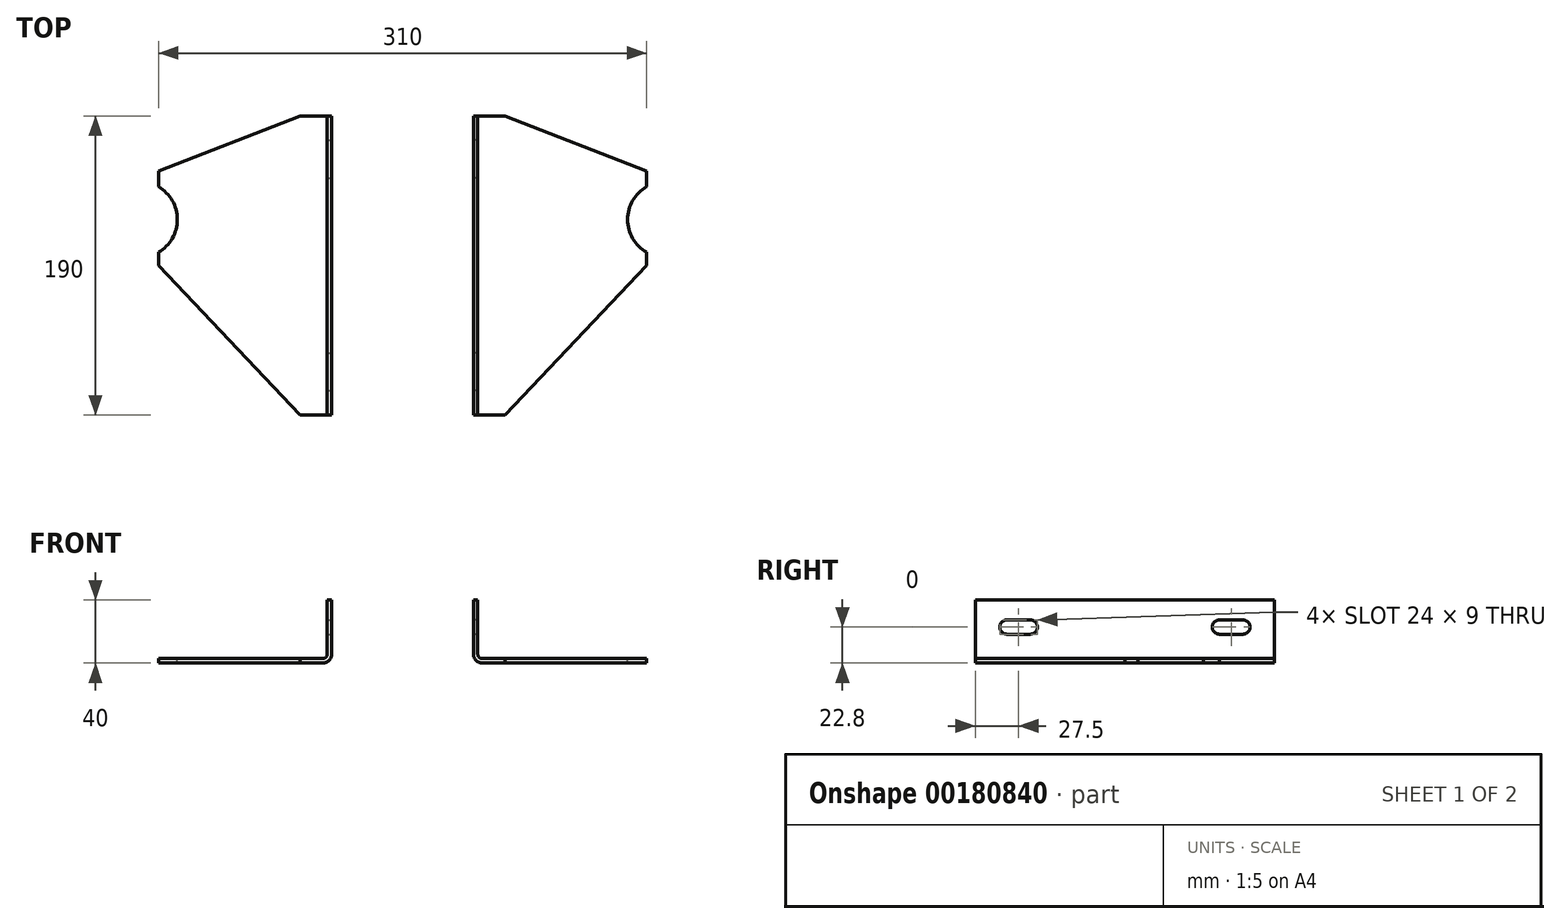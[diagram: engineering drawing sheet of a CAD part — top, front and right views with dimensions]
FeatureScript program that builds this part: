
annotation { "Feature Type Name" : "Feature", "Feature Type Description" : "" }
export const myFeature = defineFeature(function(context is Context, id is Id, definition is map)
    precondition{}
    {
        {
            var Q0;
            Q0=qCreatedBy(makeId("Front.planeOp"),FACE);
            var sketch = newSketch(context, id + "F0", { "sketchPlane" : qUnion([Q0])});
            skLineSegment(sketch, "E0", {"start": v(0, 0) * mm, "end": v(-55, 0) * mm});
            skLineSegment(sketch, "E1", {"start": v(0, 0) * mm, "end": v(49.4, 0) * mm});
            skLineSegment(sketch, "E2", {"start": v(55, 5.6) * mm, "end": v(55, 40) * mm});
            skLineSegment(sketch, "E3.0", {"start": v(52.2, 5.6) * mm, "end": v(52.2, 40) * mm});
            skLineSegment(sketch, "E4.0", {"start": v(0, 2.8) * mm, "end": v(49.4, 2.8) * mm});
            skLineSegment(sketch, "E5.0", {"start": v(0, 2.8) * mm, "end": v(-55, 2.8) * mm});
            skLineSegment(sketch, "E6", {"start": v(-55, 0) * mm, "end": v(-55, 2.8) * mm});
            skLineSegment(sketch, "E7", {"start": v(55, 40) * mm, "end": v(52.2, 40) * mm});
            skArc(sketch, "E8.filletArc", {"start": v(49.4, 2.8) * mm, "mid": v(51.38, 3.62) * mm, "end": v(52.2, 5.6) * mm});
            skPoint(sketch, "E9.visualSharp", {"position": v(55, 0) * mm});
            skArc(sketch, "E9.filletArc", {"start": v(49.4, 0) * mm, "mid": v(53.36, 1.64) * mm, "end": v(55, 5.6) * mm});
            skSolve(sketch);
        }
        {
            var Q0;
            Q0 = qSketchRegion(id + "F0", true);
            extrude(context, id + "F1", {"entities" : qUnion([Q0]), "depth" : 190 * mm});
        }
        {
            var Q0;
            Q0=makeQuery(id+"F1.opExtrude","SWEPT_FACE",FACE,{"disambiguationData":[OSD([sQuery(id+"F0.wireOp",EDGE,"E4.0"),sQuery(id+"F0.wireOp",EDGE,"E5.0")])]});
            var sketch = newSketch(context, id + "F2", { "sketchPlane" : qUnion([Q0])});
            skLineSegment(sketch, "E10", {"start": v(-55, 0) * mm, "end": v(-55, -35) * mm});
            skLineSegment(sketch, "E11", {"start": v(-55, 0) * mm, "end": v(35, 0) * mm});
            skLineSegment(sketch, "E12", {"start": v(-55, -35) * mm, "end": v(35, 0) * mm});
            skLineSegment(sketch, "E13", {"start": v(-55, -190) * mm, "end": v(-55, -95) * mm});
            skLineSegment(sketch, "E14", {"start": v(-55, -95) * mm, "end": v(35, -190) * mm});
            skLineSegment(sketch, "E15", {"start": v(-55, -190) * mm, "end": v(35, -190) * mm});
            skLineSegment(sketch, "E16.0", {"start": v(-43, -190) * mm, "end": v(-43, 0) * mm});
            skLineSegment(sketch, "E17.0", {"start": v(-55, -65.8) * mm, "end": v(35, -65.8) * mm});
            skLineSegment(sketch, "E18", {"start": v(-43, -65.8) * mm, "end": v(-55, -65.8) * mm});
            skLineSegment(sketch, "E19", {"start": v(-55, -65.8) * mm, "end": v(-67, -65.8) * mm});
            skCircle(sketch, "E20", {"center": v(-67, -65.8) * mm, "radius": 24 * mm});
            skSolve(sketch);
        }
        {
            var Q0;
            Q0 = qSketchRegion(id + "F2", true);
            extrude(context, id + "F3", {"entities" : qUnion([Q0]), "operationType" : NewBodyOperationType.REMOVE, "oppositeDirection" : true, "depth" : 3 * mm});
        }
        {
            var Q0;
            Q0=makeQuery(id+"F1.opExtrude","SWEPT_FACE",FACE,{"disambiguationData":[OSD([sQuery(id+"F0.wireOp",EDGE,"E2")])]});
            var sketch = newSketch(context, id + "F4", { "sketchPlane" : qUnion([Q0])});
            skLineSegment(sketch, "E21", {"start": v(0, 22.8) * mm, "end": v(-20, 22.8) * mm});
            skArc(sketch, "E22", {"start": v(-20, 18.3) * mm, "mid": v(-15.5, 22.8) * mm, "end": v(-20, 27.3) * mm});
            skArc(sketch, "E23", {"start": v(-35, 27.3) * mm, "mid": v(-39.5, 22.8) * mm, "end": v(-35, 18.3) * mm});
            skLineSegment(sketch, "E24", {"start": v(-35, 18.3) * mm, "end": v(-20, 18.3) * mm});
            skLineSegment(sketch, "E25", {"start": v(-35, 27.3) * mm, "end": v(-20, 27.3) * mm});
            skLineSegment(sketch, "E26", {"start": v(-95, 40) * mm, "end": v(-95, 22.42) * mm});
            skPoint(sketch, "E26.endSnap0", {"position": v(-95, 40) * mm});
            skLineSegment(sketch, "E27.MirrorCS", {"start": v(-155, 18.3) * mm, "end": v(-170, 18.3) * mm});
            skArc(sketch, "E28.MirrorCS", {"start": v(-155, 27.3) * mm, "mid": v(-150.5, 22.8) * mm, "end": v(-155, 18.3) * mm});
            skLineSegment(sketch, "E29.MirrorCS", {"start": v(-155, 27.3) * mm, "end": v(-170, 27.3) * mm});
            skArc(sketch, "E30.MirrorCS", {"start": v(-170, 18.3) * mm, "mid": v(-174.5, 22.8) * mm, "end": v(-170, 27.3) * mm});
            skSolve(sketch);
        }
        {
            var Q0;
            Q0 = qSketchRegion(id + "F4", true);
            extrude(context, id + "F5", {"entities" : qUnion([Q0]), "operationType" : NewBodyOperationType.REMOVE, "oppositeDirection" : true, "depth" : 3 * mm});
        }
        {
            var Q0;
            Q0=qCreatedBy(makeId("Right.planeOp"),FACE);
            cPlane(context, id + "F6", {"entities" : qUnion([Q0]), "cplaneType" : CPlaneType.OFFSET, "offset" : 100 * mm, "width" : 150 * mm, "height" : 150 * mm});
        }
        {
            var Q0;
            Q0=makeQuery(id+"F1.opExtrude","SWEPT_BODY",BODY,{"disambiguationData":[OSD([sQuery(id+"F0.wireOp",EDGE,"E0"),sQuery(id+"F0.wireOp",EDGE,"E1"),sQuery(id+"F0.wireOp",EDGE,"E2"),sQuery(id+"F0.wireOp",EDGE,"E3.0"),sQuery(id+"F0.wireOp",EDGE,"E4.0"),sQuery(id+"F0.wireOp",EDGE,"E5.0"),sQuery(id+"F0.wireOp",EDGE,"E6"),sQuery(id+"F0.wireOp",EDGE,"E7"),sQuery(id+"F0.wireOp",EDGE,"E8.filletArc"),sQuery(id+"F0.wireOp",EDGE,"E9.filletArc")])]});
            var Q1;
            Q1=qCreatedBy(id+"F6.planeOp",FACE);
            mirror(context, id + "F7", {"entities" : qUnion([Q0]), "mirrorPlane" : qUnion([Q1])});
        }
    });
